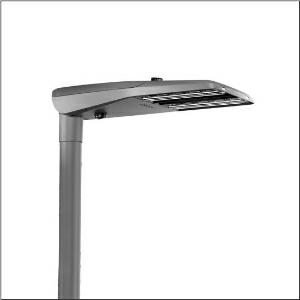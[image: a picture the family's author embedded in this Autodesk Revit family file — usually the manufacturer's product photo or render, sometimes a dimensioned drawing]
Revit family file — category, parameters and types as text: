
# Revit family: streetlight_sl_11_iq_midi___st1_0ab_5xc3n51y08me_91dd
name_source: partatom
category: Lighting Fixtures
units: mm (PartAtom-declared; Revit-internal decimal feet)

## family parameters
Cut with Voids When Loaded = No
Host = Face
Light Source = No
Part Type = Normal
Room Calculation Point = No
Round Connector Dimension = Use Diameter
Shared = No

## types (1)
- --- (1 x LED, 15260 lm, 122.7 W, 3000K)
    Apparent Load = 123 VA
    CIE Flux Codes = 29 63 95 100 100
    Color Rendering = 70
    Color Temperature = 3000K
    Default Elevation = 1800 mm
    Description = Streetlight SL 11 iQ midi, mast luminaire, primary light control with 3 zone facetted reflector, of plastic, silver coated, highly specular, primary optical cover: cover, of PMMA, transparent, light distribution: ST1.0aB, light emission: direct distribution, primary light characteristic: asymmetric, installation type: post-top, side-entry, lamps: LED, High Power LED, rated values: 15.260lm | 122,7W | 124,4lm/W (begin service life); end service life: 15.260lm | 130,2W; at 50% lumin. flux: 7.630lm | 56,1W | 136lm/W, colour temperature: 3000K, colour rendering: CRI > 70, light colour: 730, light setting 1 begin service life: 100% | 15.260lm | 122,7W | 124,4lm/W | 3.000K, light setting 1 end service life: 130,2W, further light settings possible, control: pre-setting: logarithmic dimming characteristic, Street-Remote, Auto-Match, Temp-Guard, Lumen-Switch, Night-Set, Smart-Wire, Light-Fading, Desk-Remote (wireless, voltage-free reading and setting of iQ features in the workshop via application-optimized NFC function/RFID function), optimised constant luminous flux control (CLO 2.0), with cable H07RN-F 3x 1.5mm², mains connection: 230..240V, AC, 50/60Hz, connection cable pre-assembled, cable length: 12,5m, luminaire housing, of diecast aluminium, powder-coated, SITECO metallic grey (DB 702S), please order mast flange separately, inclination adjustable without tools: 0°, 5°, 10°, 15° (post-top) | 0°, -5°, -10°, -15° (side-entry), sealing non-destructively replaceable, multi-level sealing system, length: 780mm, width: 376mm, height: 118mm, mast flange for spigot size: 42mm (side-entry): 5XC10008XM4, 60/48mm (side-entry/post-top): 5XC10108XM2, 76/60mm (side-entry/post-top): 5XC10108XM1, equipment: Power, Smart Interface below and above, protection rating (complete): IP66, insulation class (complete): insulation class II (safety insulation), certification: CE, ENEC, ENEC+, VDE, UKCA, impact resistance: IK10, permissible operating ambient temperature for outdoor applications: -25..+50°C, standard-compliant lighting for roads and squares, Environmental Product Declaration (EPD) tested and certified by an independent institute, packaging unit: 1 piece

Light Distribution: ST1.0aB
    Height = 118 mm
    Lamp = 1 x LED
    Lamp Light Flux = 15260 lm
    Lamp Power = 122.7 W
    Lamp count = 1
    Length = 780 mm
    Luminous efficacy = 124 lm/W
    Manufacturer = Siteco
    ModVariant = No
    Model = 5XC3N51Y08ME
    Number of Poles = 1
    OnlyDefault = Yes
    Power Factor = 1
    Product Name = Streetlight SL 11 iQ midi | ST1.0aB
    Product group = mast luminaire | pylon top
    ProductGroupID = 6100
    Protection Class = Protection class II
    Protection Degree = IP 66
    RLX_Detail_Level = 1
    RLX_Emergency_Light_Flux = 0 lm
    RLX_Emergency_Type = 0
    RLX_Emergency_Type_DB = No
    RlxData = <blob elided: 69481 chars, md5=26b736ec>
    Socket = socket
    Standby Power = 0 W
    System Light Flux = 15260 lm
    System Power = 123 W
    Type Comments = factory setting: luminous flux: 100 % | dim-lin: 254 | 552 mA
    Type Image = l_1004429.jpg
    URL = http://relux.com
    VarID = @adj_091705
    Voltage = 0 V
    Weight = 0.00 kg
    Width = 376 mm

## geometry (parser evidence)
native form markers: Blend x4, Sweep x12
no freeform markers — native parametric forms only
